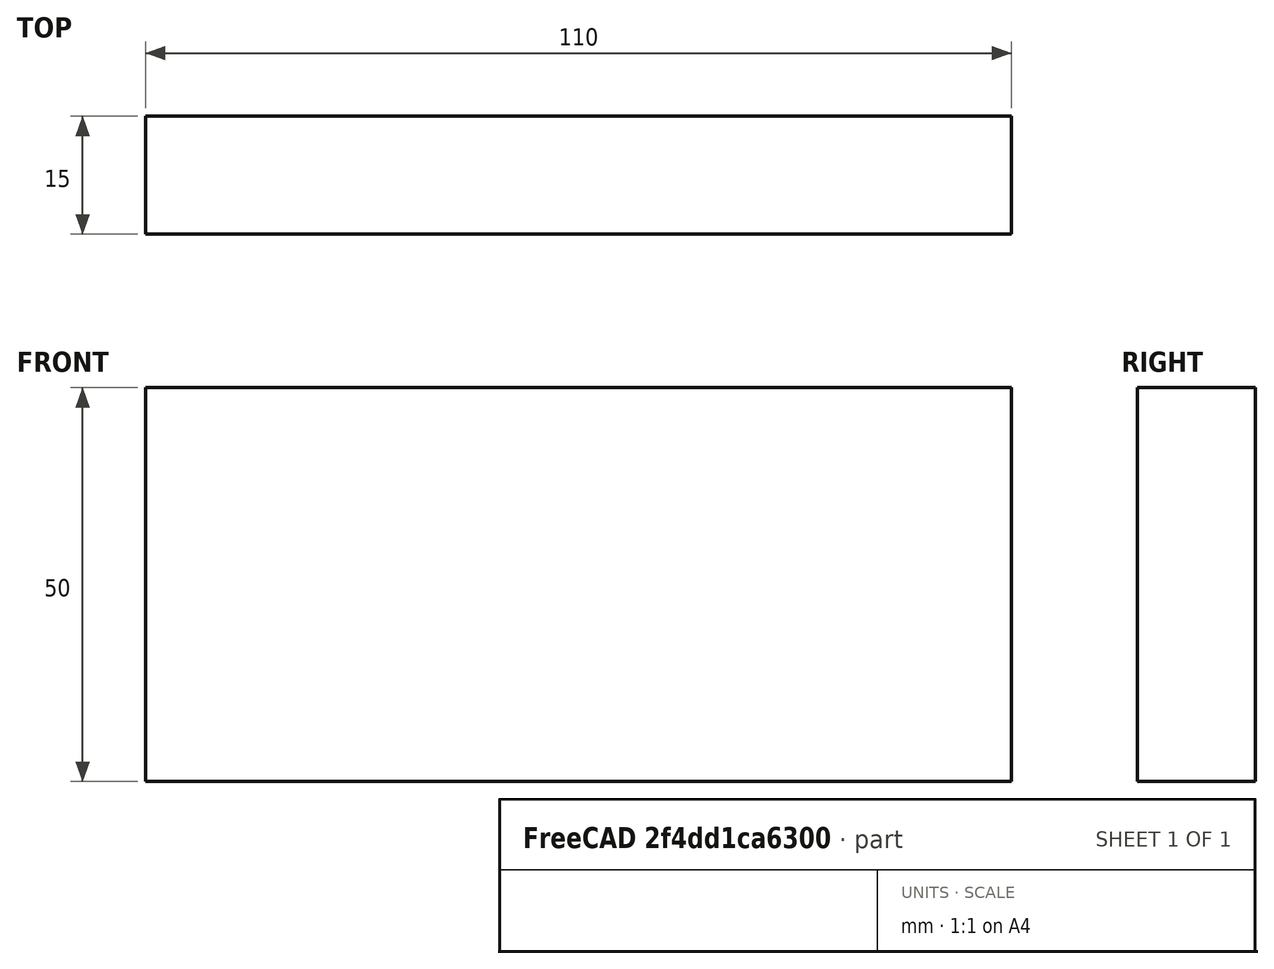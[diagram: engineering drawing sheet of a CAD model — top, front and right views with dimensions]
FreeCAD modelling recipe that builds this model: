
FCSTD DOCUMENT  (FreeCAD 0.15R4671 (Git))
Label: Flat Bar 110x15 EN10058 S235JR
License: All rights reserved
LicenseURL: http://en.wikipedia.org/wiki/All_rights_reserved
objects: Sketcher::SketchObject×1, Part::Extrusion×1
note: 2 computed .brp shape members not serialized (recipe doc carries the construction recipe); baked Part::Feature solids carry a one-line shape summary decoded from their .brp

FEATURE [Sketcher::SketchObject] Sketch
  sketch-geometry (4):
    g0: LineSegment StartX=-55 StartY=-7.5 StartZ=0 EndX=55 EndY=-7.5 EndZ=0
    g1: LineSegment StartX=55 StartY=-7.5 StartZ=0 EndX=55 EndY=7.5 EndZ=0
    g2: LineSegment StartX=55 StartY=7.5 StartZ=0 EndX=-55 EndY=7.5 EndZ=0
    g3: LineSegment StartX=-55 StartY=7.5 StartZ=0 EndX=-55 EndY=-7.5 EndZ=0
  constraints (12):
    c: Coincident(g0,g1)
    c: Coincident(g1,g2)
    c: Coincident(g2,g3)
    c: Coincident(g3,g0)
    c: Horizontal(g0)
    c: Horizontal(g2)
    c: Vertical(g1)
    c: Vertical(g3)
    c: Symmetric(g1,g2,g-2)
    c: Symmetric(g0,g1,g-1)
    c: DistanceY(g1) = 15
    c: DistanceX(g0) = 110
FEATURE [Part::Extrusion] Extrude  label="Flat Bar 110x15 EN10058 S235JR"
  Base = -> Sketch
  Dir = (0,0,50)
  Solid = true
